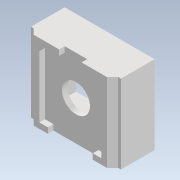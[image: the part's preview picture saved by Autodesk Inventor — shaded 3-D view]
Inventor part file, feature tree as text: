
AUTODESK INVENTOR PART (.ipt)
format: ipt  version: 2020.2 (Build 242310000, 310)  size: 156,160 bytes
history: native  units: mm
features: extrude x4, sketch x4, chamfer x2
ambient origin geometry x8: Origin, YZ Plane, XZ Plane, XY Plane, X Axis, Y Axis, Z Axis, Center Point
bodies: Solid1 (feature_tree)
feature tree (10):
  extrude  "Extrusion1"  Depth=10.0mm
  extrude  "Extrusion2"  Depth=5.0mm TaperAngle=0.0deg
  extrude  "Extrusion3"  Depth=5.0mm
  chamfer  "Chamfer1"  Distance=12.0mm
  chamfer  "Chamfer2"  Distance=1.0mm
  extrude  "Extrusion4"  Depth=2.0mm
  sketch  "Sketch1"  dims[d0=12.0mm d1=10.0mm]
  sketch  "Sketch2"  dims[d2=2.0mm d3=5.0mm d4=0.0mm]
  sketch  "Sketch3"  dims[d5=1.0mm d6=0.0mm d7=5.0mm]
  sketch  "Sketch4"  dims[d8=11.0mm d9=12.0mm d10=1.0mm d11=2.0mm d12=2.0mm d13=4.0mm d14=4.0mm d15=1.0mm d16=0.0mm d17=1.0mm d18=2.0mm d19=45.0deg d20=3.0mm d21=2.0mm d22=45.0deg d23=1.2mm d24=1.2mm d25=5.5mm d26=9.0mm d27=2.0mm d28=0.0mm]
